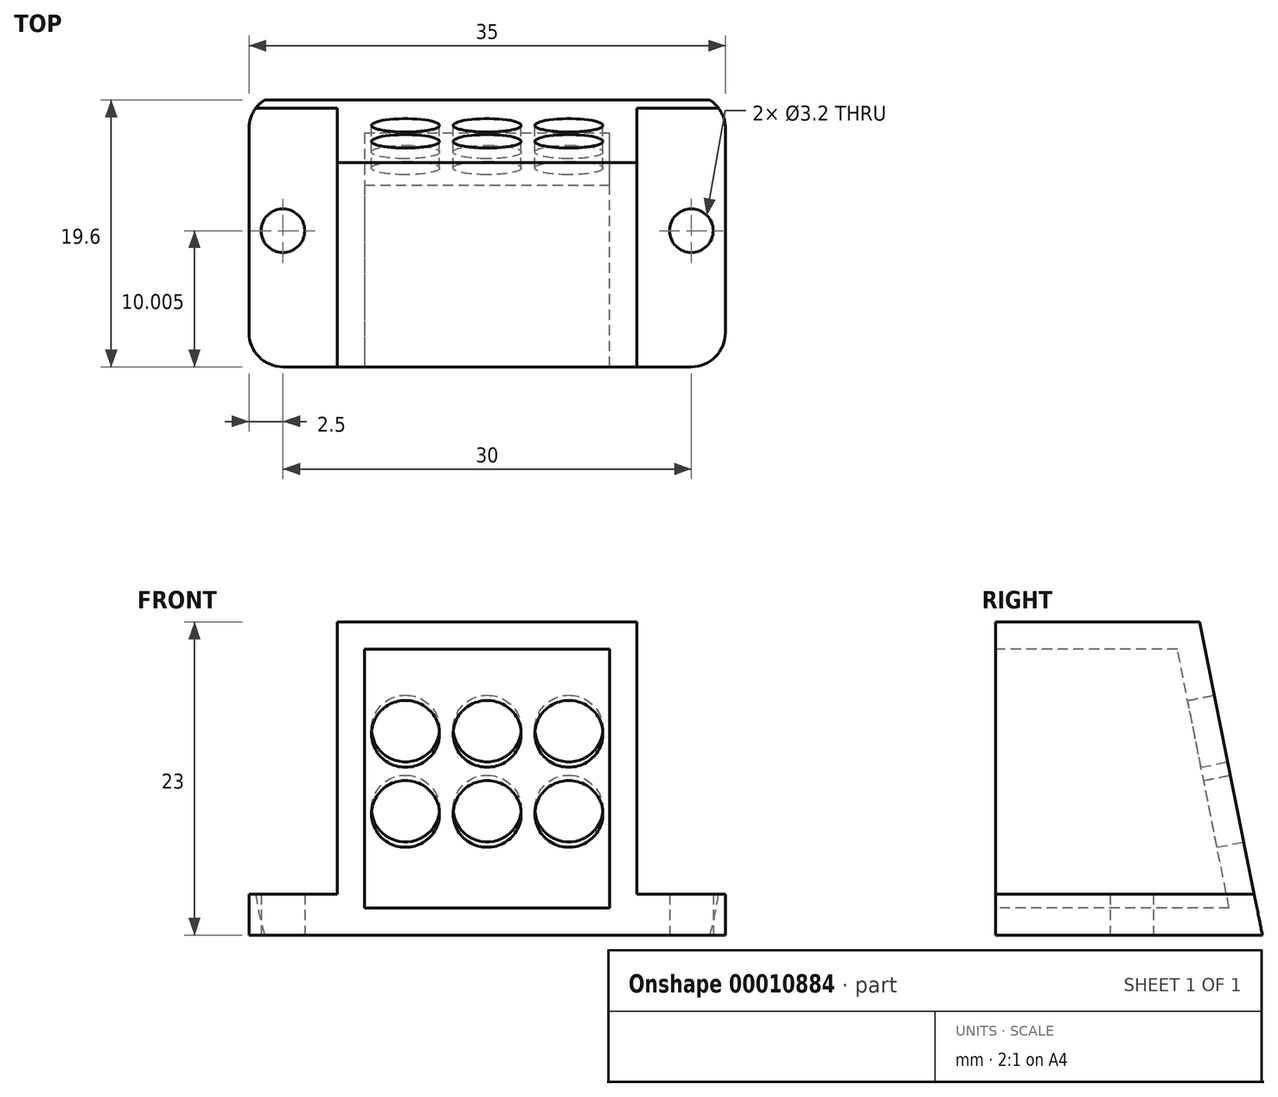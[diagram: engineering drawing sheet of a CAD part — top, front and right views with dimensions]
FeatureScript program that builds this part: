
annotation { "Feature Type Name" : "Feature", "Feature Type Description" : "" }
export const myFeature = defineFeature(function(context is Context, id is Id, definition is map)
    precondition{}
    {
        {
            var Q0;
            Q0=qCreatedBy(makeId("Top.planeOp"),FACE);
            var sketch = newSketch(context, id + "F0", { "sketchPlane" : qUnion([Q0])});
            skLineSegment(sketch, "E0.top", {"start": v(-15, 12.63) * mm, "end": v(15, 12.63) * mm});
            skLineSegment(sketch, "E0.left", {"start": v(-17.5, -4.87) * mm, "end": v(-17.5, 10.13) * mm});
            skLineSegment(sketch, "E0.right", {"start": v(17.5, -4.87) * mm, "end": v(17.5, 10.13) * mm});
            skLineSegment(sketch, "E1", {"start": v(-15, -7.37) * mm, "end": v(15, -7.37) * mm});
            skPoint(sketch, "E2.visualSharp", {"position": v(-17.5, -7.37) * mm});
            skArc(sketch, "E2.filletArc", {"start": v(-17.5, -4.87) * mm, "mid": v(-16.77, -6.63) * mm, "end": v(-15, -7.37) * mm});
            skPoint(sketch, "E3.visualSharp", {"position": v(17.5, -7.37) * mm});
            skArc(sketch, "E3.filletArc", {"start": v(15, -7.37) * mm, "mid": v(16.77, -6.63) * mm, "end": v(17.5, -4.87) * mm});
            skLineSegment(sketch, "E4.bottom", {"start": v(11, -3.15) * mm, "end": v(-11, -3.15) * mm, "construction": true});
            skLineSegment(sketch, "E4.top", {"start": v(11, 3.15) * mm, "end": v(-11, 3.15) * mm, "construction": true});
            skLineSegment(sketch, "E4.left", {"start": v(11, -3.15) * mm, "end": v(11, 3.15) * mm, "construction": true});
            skLineSegment(sketch, "E4.right", {"start": v(-11, -3.15) * mm, "end": v(-11, 3.15) * mm, "construction": true});
            skLineSegment(sketch, "E5", {"start": v(11, 3.15) * mm, "end": v(-11, -3.15) * mm, "construction": true});
            skPoint(sketch, "E6", {"position": v(0, 0) * mm});
            skCircle(sketch, "E7", {"center": v(15, 2.63) * mm, "radius": 1.6 * mm});
            skCircle(sketch, "E8", {"center": v(-15, 2.63) * mm, "radius": 1.6 * mm});
            skLineSegment(sketch, "E9", {"start": v(0, 12.63) * mm, "end": v(0, 0) * mm, "construction": true});
            skLineSegment(sketch, "E10", {"start": v(15, 2.63) * mm, "end": v(-15, 2.63) * mm, "construction": true});
            skPoint(sketch, "E11", {"position": v(0, 2.63) * mm});
            skPoint(sketch, "E12.visualSharp", {"position": v(17.5, 12.63) * mm});
            skArc(sketch, "E12.filletArc", {"start": v(17.5, 10.13) * mm, "mid": v(16.77, 11.9) * mm, "end": v(15, 12.63) * mm});
            skPoint(sketch, "E13.visualSharp", {"position": v(-17.5, 12.63) * mm});
            skArc(sketch, "E13.filletArc", {"start": v(-15, 12.63) * mm, "mid": v(-16.77, 11.9) * mm, "end": v(-17.5, 10.13) * mm});
            skSolve(sketch);
        }
        {
            var Q0;
            Q0 = qSketchRegion(id + "F0", true);
            extrude(context, id + "F1", {"entities" : qUnion([Q0]), "depth" : 3 * mm});
        }
        {
            var Q0;
            Q0=makeQuery(id+"F1.opExtrude","CAP_FACE",FACE,{"disambiguationData":[OSD([sQuery(id+"F0.wireOp",EDGE,"E0.bottom"),sQuery(id+"F0.wireOp",EDGE,"E0.top"),sQuery(id+"F0.wireOp",EDGE,"E0.left"),sQuery(id+"F0.wireOp",EDGE,"E0.right"),sQuery(id+"F0.wireOp",EDGE,"bf315fc5-2e13-4354-9d9b-1abd20b0f2e7"),sQuery(id+"F0.wireOp",EDGE,"56c0b484-9f82-4461-948e-a15f5c2970ef"),sQuery(id+"F0.wireOp",EDGE,"9137425a-d813-4728-b74c-ff4d19e16d59.left"),sQuery(id+"F0.wireOp",EDGE,"9137425a-d813-4728-b74c-ff4d19e16d59.right"),sQuery(id+"F0.wireOp",EDGE,"a7bf2cb3-b126-4379-8e6a-cbab06eba32f"),sQuery(id+"F0.wireOp",EDGE,"903a940f-de1d-455a-bafc-811186ec4754.trimOffspring")])],"isStart":false});
            var sketch = newSketch(context, id + "F2", { "sketchPlane" : qUnion([Q0])});
            skLineSegment(sketch, "E14.bottom", {"start": v(11, 12.63) * mm, "end": v(-11, 12.63) * mm});
            skPoint(sketch, "E15", {"position": v(0, 12.63) * mm});
            skLineSegment(sketch, "E16", {"start": v(-11, 12.63) * mm, "end": v(-11, -7.37) * mm});
            skLineSegment(sketch, "E17", {"start": v(-11, -7.37) * mm, "end": v(11, -7.37) * mm});
            skLineSegment(sketch, "E18", {"start": v(11, -7.37) * mm, "end": v(11, 12.63) * mm});
            skSolve(sketch);
        }
        {
            var Q0;
            Q0 = qSketchRegion(id + "F2", true);
            extrude(context, id + "F3", {"entities" : qUnion([Q0]), "operationType" : NewBodyOperationType.ADD, "depth" : 20 * mm});
        }
        {
            var Q0;
            Q0=makeQuery(id+"F3.opExtrude","CAP_EDGE",EDGE,{"disambiguationData":[OSD([sQuery(id+"F2.wireOp",EDGE,"E14.bottom")])],"isStart":false});
            chamfer(context, id + "F4", {"entities" : qUnion([Q0]), "chamferType" : ChamferType.TWO_OFFSETS, "width1" : 5 * mm, "oppositeDirection" : true, "width2" : 25 * mm, "tangentPropagation" : true});
        }
        {
            var Q0;
            Q0=makeQuery(id+"F4.opChamfer","BLEND_FACE",FACE,{"disambiguationData":[OSD([sQuery(id+"F2.wireOp",EDGE,"E14.bottom")])]});
            var sketch = newSketch(context, id + "F5", { "sketchPlane" : qUnion([Q0])});
            skLineSegment(sketch, "E19.bottom", {"start": v(6, 7.08) * mm, "end": v(-6, 7.08) * mm, "construction": true});
            skLineSegment(sketch, "E19.top", {"start": v(6, 13.08) * mm, "end": v(-6, 13.08) * mm, "construction": true});
            skLineSegment(sketch, "E19.left", {"start": v(6, 7.08) * mm, "end": v(6, 13.08) * mm, "construction": true});
            skLineSegment(sketch, "E19.right", {"start": v(-6, 7.08) * mm, "end": v(-6, 13.08) * mm, "construction": true});
            skLineSegment(sketch, "E20", {"start": v(0, 7.08) * mm, "end": v(0, 0) * mm, "construction": true});
            skCircle(sketch, "E21", {"center": v(-6, 7.08) * mm, "radius": 2.5 * mm});
            skCircle(sketch, "E22", {"center": v(-6, 13.08) * mm, "radius": 2.5 * mm});
            skCircle(sketch, "E23", {"center": v(6, 13.08) * mm, "radius": 2.5 * mm});
            skCircle(sketch, "E24", {"center": v(6, 7.08) * mm, "radius": 2.5 * mm});
            skLineSegment(sketch, "E25", {"start": v(0, 7.08) * mm, "end": v(0, 13.08) * mm, "construction": true});
            skCircle(sketch, "E26", {"center": v(0, 7.08) * mm, "radius": 2.5 * mm});
            skCircle(sketch, "E27", {"center": v(0, 13.08) * mm, "radius": 2.5 * mm});
            skSolve(sketch);
        }
        {
            var Q0;
            Q0=makeQuery(id+"F3.opExtrude","SWEPT_FACE",FACE,{"disambiguationData":[OSD([sQuery(id+"F2.wireOp",EDGE,"E17")])]});
            shell(context, id + "F6", {"entities" : qUnion([Q0]), "thickness" : 2 * mm});
        }
        {
            var Q0;
            Q0 = qSketchRegion(id + "F5", true);
            extrude(context, id + "F7", {"entities" : qUnion([Q0]), "operationType" : NewBodyOperationType.REMOVE, "endBound" : BoundingType.THROUGH_ALL, "oppositeDirection" : true, "depth" : 25 * mm});
        }
    });
